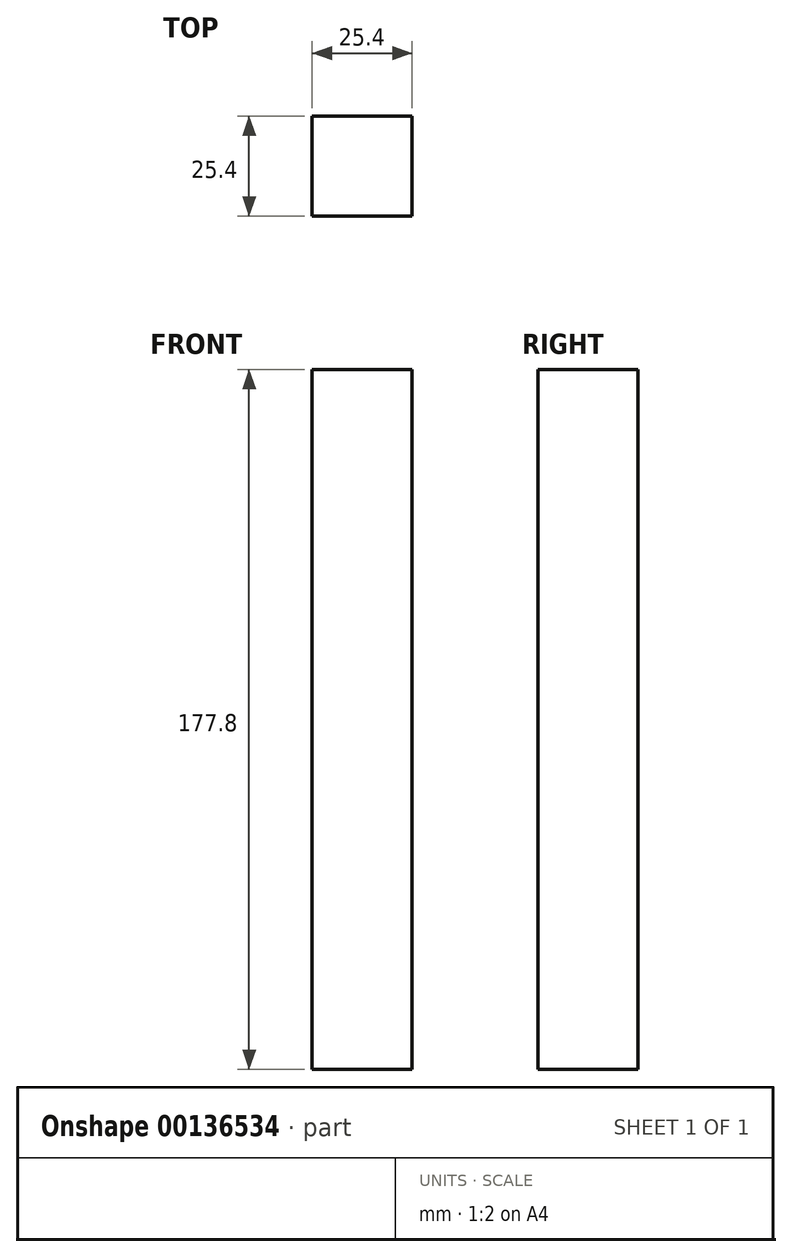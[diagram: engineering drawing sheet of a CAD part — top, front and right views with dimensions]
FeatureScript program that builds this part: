
annotation { "Feature Type Name" : "Feature", "Feature Type Description" : "" }
export const myFeature = defineFeature(function(context is Context, id is Id, definition is map)
    precondition{}
    {
        {
            var Q0;
            Q0=qCreatedBy(makeId("Top.planeOp"),FACE);
            var sketch = newSketch(context, id + "F0", { "sketchPlane" : qUnion([Q0])});
            skLineSegment(sketch, "E0.bottom", {"start": v(12.7, -12.7) * mm, "end": v(-12.7, -12.7) * mm});
            skLineSegment(sketch, "E0.top", {"start": v(12.7, 12.7) * mm, "end": v(-12.7, 12.7) * mm});
            skLineSegment(sketch, "E0.left", {"start": v(12.7, -12.7) * mm, "end": v(12.7, 12.7) * mm});
            skLineSegment(sketch, "E0.right", {"start": v(-12.7, -12.7) * mm, "end": v(-12.7, 12.7) * mm});
            skPoint(sketch, "E0.middle", {"position": v(0, 0) * mm});
            skSolve(sketch);
        }
        {
            var Q0;
            Q0 = qSketchRegion(id + "F0", true);
            extrude(context, id + "F1", {"entities" : qUnion([Q0]), "depth" : 177.8 * mm});
        }
    });
